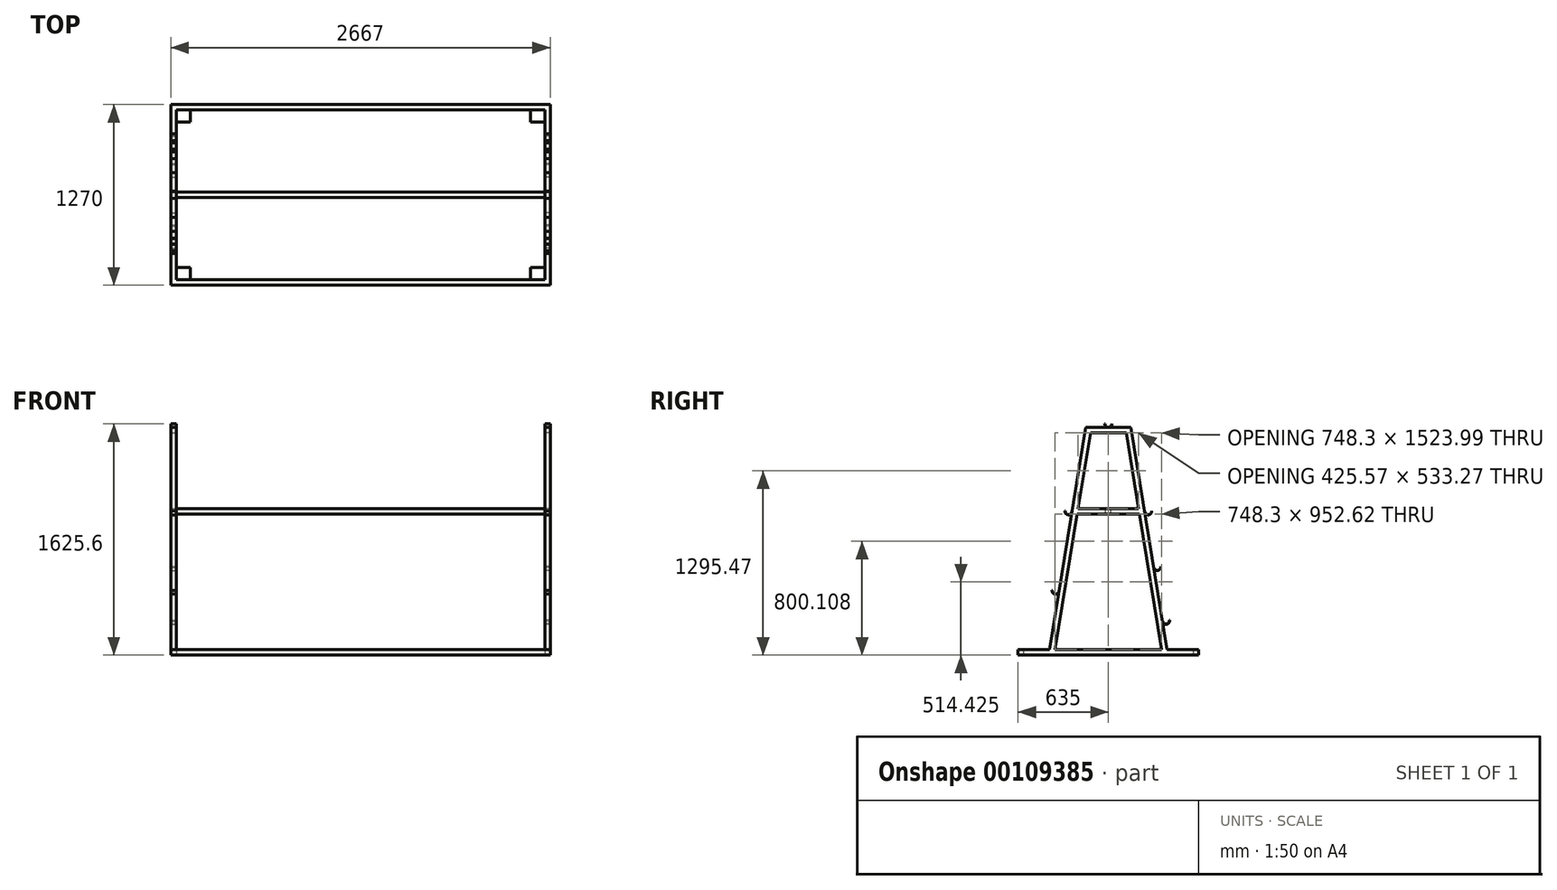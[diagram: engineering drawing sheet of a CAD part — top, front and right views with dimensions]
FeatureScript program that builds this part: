
annotation { "Feature Type Name" : "Feature", "Feature Type Description" : "" }
export const myFeature = defineFeature(function(context is Context, id is Id, definition is map)
    precondition{}
    {
        {
            var Q0;
            Q0=qCreatedBy(makeId("Right.planeOp"),FACE);
            cPlane(context, id + "F0", {"entities" : qUnion([Q0]), "cplaneType" : CPlaneType.OFFSET, "offset" : 1295.4 * mm, "oppositeDirection" : true, "width" : 152.4 * mm, "height" : 152.4 * mm});
        }
        {
            var Q0;
            Q0=qCreatedBy(makeId("Right.planeOp"),FACE);
            var sketch = newSketch(context, id + "F1", { "sketchPlane" : qUnion([Q0])});
            skPoint(sketch, "E0.orphan", {"position": v(0, -38.09) * mm});
            skLineSegment(sketch, "E1.MirrorCS", {"start": v(374.15, 0.02) * mm, "end": v(219, 952.64) * mm});
            skLineSegment(sketch, "E2.trimOffspring", {"start": v(212.79, 990.74) * mm, "end": v(125.93, 1524.01) * mm});
            skLineSegment(sketch, "E3.trimOffspring", {"start": v(412.75, 0.01) * mm, "end": v(635, 0.01) * mm});
            skLineSegment(sketch, "E4.MirrorCS", {"start": v(635, 0.01) * mm, "end": v(635, -38.09) * mm});
            skLineSegment(sketch, "E5", {"start": v(0, 0) * mm, "end": v(0, 1562.11) * mm, "construction": true});
            skLineSegment(sketch, "E6", {"start": v(0, 0.02) * mm, "end": v(374.15, 0.02) * mm});
            skLineSegment(sketch, "E7", {"start": v(158.3, 1562.11) * mm, "end": v(412.75, 0.01) * mm});
            skLineSegment(sketch, "E8.0", {"start": v(0, 1562.11) * mm, "end": v(158.3, 1562.11) * mm});
            skLineSegment(sketch, "E9.trimOffspring", {"start": v(0, 1524) * mm, "end": v(125.93, 1524.01) * mm});
            skLineSegment(sketch, "E10.trimOffspring", {"start": v(0, 990.74) * mm, "end": v(212.79, 990.74) * mm});
            skLineSegment(sketch, "E11.trimOffspring", {"start": v(0, 952.64) * mm, "end": v(219, 952.64) * mm});
            skLineSegment(sketch, "E12", {"start": v(635, -38.09) * mm, "end": v(0, -38.09) * mm});
            skLineSegment(sketch, "E13.trimOffspring", {"start": v(0, 971.7) * mm, "end": v(280.2, 971.7) * mm, "construction": true});
            skLineSegment(sketch, "E14.0", {"start": v(0, 1587.51) * mm, "end": v(158.3, 1587.51) * mm, "construction": true});
            skCircle(sketch, "E15", {"center": v(0, 1587.51) * mm, "radius": 381 * mm, "construction": true});
            skLineSegment(sketch, "E16.0", {"start": v(183.36, 1566.2) * mm, "end": v(437.82, 4.1) * mm, "construction": true});
            skCircle(sketch, "E17", {"center": v(280.2, 971.7) * mm, "radius": 152.4 * mm, "construction": true});
            skLineSegment(sketch, "E18", {"start": v(318.63, 577.82) * mm, "end": v(343.7, 581.9) * mm, "construction": true});
            skCircle(sketch, "E19", {"center": v(343.7, 581.9) * mm, "radius": 152.4 * mm, "construction": true});
            skLineSegment(sketch, "E20", {"start": v(380.13, 200.26) * mm, "end": v(405.2, 204.34) * mm, "construction": true});
            skCircle(sketch, "E21", {"center": v(405.2, 204.34) * mm, "radius": 152.4 * mm, "construction": true});
            skLineSegment(sketch, "E22.MirrorCS", {"start": v(0, 1524) * mm, "end": v(-125.93, 1524.01) * mm});
            skLineSegment(sketch, "E23.MirrorCS", {"start": v(0, 1562.11) * mm, "end": v(-158.3, 1562.11) * mm});
            skLineSegment(sketch, "E24.MirrorCS", {"start": v(-158.3, 1562.11) * mm, "end": v(-412.75, 0.01) * mm});
            skLineSegment(sketch, "E25.MirrorCS", {"start": v(-212.79, 990.74) * mm, "end": v(-125.93, 1524.01) * mm});
            skLineSegment(sketch, "E26.MirrorCS", {"start": v(-183.36, 1566.2) * mm, "end": v(-437.82, 4.1) * mm, "construction": true});
            skLineSegment(sketch, "E27.MirrorCS", {"start": v(0, 990.74) * mm, "end": v(-212.79, 990.74) * mm});
            skLineSegment(sketch, "E28.MirrorCS", {"start": v(0, 971.7) * mm, "end": v(-280.2, 971.7) * mm, "construction": true});
            skLineSegment(sketch, "E29.MirrorCS", {"start": v(0, 952.64) * mm, "end": v(-219, 952.64) * mm});
            skLineSegment(sketch, "E30.MirrorCS", {"start": v(-374.15, 0.02) * mm, "end": v(-219, 952.64) * mm});
            skLineSegment(sketch, "E31.MirrorCS", {"start": v(0, 0.02) * mm, "end": v(-374.15, 0.02) * mm});
            skLineSegment(sketch, "E32.MirrorCS", {"start": v(-412.75, 0.01) * mm, "end": v(-635, 0.01) * mm});
            skLineSegment(sketch, "E33.MirrorCS", {"start": v(-635, -38.09) * mm, "end": v(0, -38.09) * mm});
            skLineSegment(sketch, "E34.MirrorCS", {"start": v(-635, 0.01) * mm, "end": v(-635, -38.09) * mm});
            skCircle(sketch, "E35", {"center": v(-280.2, 971.7) * mm, "radius": 152.4 * mm, "construction": true});
            skLineSegment(sketch, "E36", {"start": v(-345.67, 411.84) * mm, "end": v(-370.74, 415.92) * mm, "construction": true});
            skCircle(sketch, "E37", {"center": v(-370.74, 415.92) * mm, "radius": 304.8 * mm, "construction": true});
            skSolve(sketch);
        }
        {
            var Q0;
            Q0=qSketchRegion(id+"F1",true);
            extrude(context, id + "F2", {"entities" : qUnion([Q0]), "depth" : 38.1 * mm});
        }
        {
            var Q0;
            Q0=makeQuery(id+"F2.opExtrude","SWEPT_BODY",BODY,{"disambiguationData":[OSD([sQuery(id+"F1.wireOp",EDGE,"6WKcqqnf-Tb74-KSXB-T6S0-m3pTTAEzESJp"),sQuery(id+"F1.wireOp",EDGE,"1c0d4eef-4907-47d0-8670-4b10d3ef4e6d0.MirrorCS"),sQuery(id+"F1.wireOp",EDGE,"c0db719b-abba-4705-9bd6-14fd0828cea8.0"),sQuery(id+"F1.wireOp",EDGE,"tZbaEvzS-Xn5Q-mfHi-VXqp-jMpdNEXuN0R4"),sQuery(id+"F1.wireOp",EDGE,"rspVW4E9-zQsA-o8DC-rcqs-QNP9QNG2WVSy"),sQuery(id+"F1.wireOp",EDGE,"08289d95-367d-4b9a-ab30-8cc4f747b8f0.0"),sQuery(id+"F1.wireOp",EDGE,"3ac95e61-57ea-43e8-b189-1b48f2394685.0"),sQuery(id+"F1.wireOp",EDGE,"d8f0bd9f-68f3-4107-a600-d1b0ad9bb81b0.MirrorCS"),sQuery(id+"F1.wireOp",EDGE,"E1.MirrorCS"),sQuery(id+"F1.wireOp",EDGE,"a417d048-553f-458f-8e46-2cb23e010311.0"),sQuery(id+"F1.wireOp",EDGE,"5fd8f543-2721-4fe0-ad3b-1b1c11d777a4.0"),sQuery(id+"F1.wireOp",EDGE,"c230fa98-fb04-4ea0-a6fe-6f0d8f7d4e36.trimOffspring"),sQuery(id+"F1.wireOp",EDGE,"74a05f44-4bf8-40a7-b958-81660b9f7f5f.trimOffspring"),sQuery(id+"F1.wireOp",EDGE,"a848d9df-170e-4563-af66-a8ff7f0327df.trimOffspring"),sQuery(id+"F1.wireOp",EDGE,"E2.trimOffspring"),sQuery(id+"F1.wireOp",EDGE,"84869966-22ca-4afa-a9a6-1a304451bc45.trimOffspring"),sQuery(id+"F1.wireOp",EDGE,"E3.trimOffspring")])]});
            var Q1;
            Q1=qCreatedBy(id+"F0.planeOp",FACE);
            mirror(context, id + "F3", {"entities" : qUnion([Q0]), "mirrorPlane" : qUnion([Q1])});
        }
        {
            var Q0;
            Q0=qCreatedBy(makeId("Right.planeOp"),FACE);
            var sketch = newSketch(context, id + "F4", { "sketchPlane" : qUnion([Q0])});
            skPoint(sketch, "E38.orphan", {"position": v(254.47, 971.68) * mm});
            skArc(sketch, "E39", {"start": v(254.55, 971.69) * mm, "mid": v(281.9, 948.4) * mm, "end": v(305.2, 975.76) * mm});
            skLineSegment(sketch, "E40", {"start": v(254.47, 971.68) * mm, "end": v(256.58, 971.85) * mm});
            skArc(sketch, "E41.0", {"start": v(256.58, 971.85) * mm, "mid": v(281.75, 950.43) * mm, "end": v(303.17, 975.6) * mm});
            skLineSegment(sketch, "E42.trimOffspring", {"start": v(303.17, 975.6) * mm, "end": v(305.2, 975.76) * mm});
            skLineSegment(sketch, "E43", {"start": v(428.26, 208.1) * mm, "end": v(430.27, 208.43) * mm});
            skLineSegment(sketch, "E44.0", {"start": v(183.36, 1566.2) * mm, "end": v(437.82, 4.08) * mm, "construction": true});
            skLineSegment(sketch, "E45", {"start": v(318.63, 577.82) * mm, "end": v(320.63, 578.15) * mm});
            skArc(sketch, "E46", {"start": v(318.63, 577.82) * mm, "mid": v(347.78, 556.83) * mm, "end": v(368.77, 585.99) * mm});
            skArc(sketch, "E47.0", {"start": v(320.63, 578.15) * mm, "mid": v(347.46, 558.84) * mm, "end": v(366.76, 585.66) * mm});
            skLineSegment(sketch, "E48.trimOffspring", {"start": v(366.76, 585.66) * mm, "end": v(368.77, 585.99) * mm});
            skArc(sketch, "E49", {"start": v(380.13, 200.26) * mm, "mid": v(409.28, 179.27) * mm, "end": v(430.27, 208.43) * mm});
            skArc(sketch, "E50.0", {"start": v(382.14, 200.59) * mm, "mid": v(408.96, 181.28) * mm, "end": v(428.26, 208.1) * mm});
            skPoint(sketch, "E51.orphan", {"position": v(380.13, 200.26) * mm});
            skLineSegment(sketch, "E52.trimOffspring", {"start": v(382.14, 200.59) * mm, "end": v(380.13, 200.26) * mm});
            skLineSegment(sketch, "E53.MirrorCS", {"start": v(-254.47, 971.68) * mm, "end": v(-256.58, 971.85) * mm});
            skLineSegment(sketch, "E54.MirrorCS", {"start": v(-303.17, 975.6) * mm, "end": v(-305.2, 975.76) * mm});
            skArc(sketch, "E55.MirrorCS", {"start": v(-256.58, 971.85) * mm, "mid": v(-281.75, 950.43) * mm, "end": v(-303.17, 975.6) * mm});
            skPoint(sketch, "E56.MirrorP", {"position": v(-254.47, 971.68) * mm});
            skArc(sketch, "E57.MirrorCS", {"start": v(-254.55, 971.69) * mm, "mid": v(-281.9, 948.4) * mm, "end": v(-305.2, 975.76) * mm});
            skLineSegment(sketch, "E58.MirrorCS", {"start": v(-183.36, 1566.2) * mm, "end": v(-437.82, 4.08) * mm, "construction": true});
            skLineSegment(sketch, "E59.MirrorCS", {"start": v(-345.33, 413.88) * mm, "end": v(-347.44, 414.05) * mm});
            skLineSegment(sketch, "E60.MirrorCS", {"start": v(-394.03, 417.8) * mm, "end": v(-396.05, 417.95) * mm});
            skArc(sketch, "E61.MirrorCS", {"start": v(-347.44, 414.05) * mm, "mid": v(-372.6, 392.63) * mm, "end": v(-394.03, 417.8) * mm});
            skPoint(sketch, "E62.MirrorP", {"position": v(-345.33, 413.88) * mm});
            skArc(sketch, "E63.MirrorCS", {"start": v(-345.42, 413.88) * mm, "mid": v(-372.77, 390.6) * mm, "end": v(-396.05, 417.95) * mm});
            skArc(sketch, "E64", {"start": v(-25.4, 1587.51) * mm, "mid": v(0, 1562.11) * mm, "end": v(25.4, 1587.51) * mm});
            skArc(sketch, "E65.0", {"start": v(-23.37, 1587.51) * mm, "mid": v(0, 1564.14) * mm, "end": v(23.37, 1587.51) * mm});
            skLineSegment(sketch, "E66", {"start": v(25.4, 1587.51) * mm, "end": v(23.37, 1587.51) * mm});
            skLineSegment(sketch, "E67.trimOffspring", {"start": v(-23.37, 1587.51) * mm, "end": v(-25.4, 1587.51) * mm});
            skSolve(sketch);
        }
        {
            var Q0;
            Q0 = qSketchRegion(id + "F4", true);
            extrude(context, id + "F5", {"entities" : qUnion([Q0]), "depth" : 38.1 * mm});
        }
        {
            var Q0;
            Q0=makeQuery(id+"F5.opExtrude","SWEPT_BODY",BODY,{"disambiguationData":[OSD([sQuery(id+"F4.wireOp",EDGE,"E53.MirrorCS"),sQuery(id+"F4.wireOp",EDGE,"E54.MirrorCS"),sQuery(id+"F4.wireOp",EDGE,"E55.MirrorCS"),sQuery(id+"F4.wireOp",EDGE,"E57.MirrorCS")])]});
            var Q1;
            Q1=makeQuery(id+"F5.opExtrude","SWEPT_BODY",BODY,{"disambiguationData":[OSD([sQuery(id+"F4.wireOp",EDGE,"E59.MirrorCS"),sQuery(id+"F4.wireOp",EDGE,"E60.MirrorCS"),sQuery(id+"F4.wireOp",EDGE,"E61.MirrorCS"),sQuery(id+"F4.wireOp",EDGE,"E63.MirrorCS")])]});
            var Q2;
            Q2=makeQuery(id+"F5.opExtrude","SWEPT_BODY",BODY,{"disambiguationData":[OSD([sQuery(id+"F4.wireOp",EDGE,"E64"),sQuery(id+"F4.wireOp",EDGE,"E65.0"),sQuery(id+"F4.wireOp",EDGE,"E66"),sQuery(id+"F4.wireOp",EDGE,"E67.trimOffspring")])]});
            var Q3;
            Q3=makeQuery(id+"F5.opExtrude","SWEPT_BODY",BODY,{"disambiguationData":[OSD([sQuery(id+"F4.wireOp",EDGE,"E39"),sQuery(id+"F4.wireOp",EDGE,"E40"),sQuery(id+"F4.wireOp",EDGE,"E41.0"),sQuery(id+"F4.wireOp",EDGE,"E42.trimOffspring")])]});
            var Q4;
            Q4=makeQuery(id+"F5.opExtrude","SWEPT_BODY",BODY,{"disambiguationData":[OSD([sQuery(id+"F4.wireOp",EDGE,"E45"),sQuery(id+"F4.wireOp",EDGE,"E46"),sQuery(id+"F4.wireOp",EDGE,"E47.0"),sQuery(id+"F4.wireOp",EDGE,"E48.trimOffspring")])]});
            var Q5;
            Q5=makeQuery(id+"F5.opExtrude","SWEPT_BODY",BODY,{"disambiguationData":[OSD([sQuery(id+"F4.wireOp",EDGE,"E43"),sQuery(id+"F4.wireOp",EDGE,"E49"),sQuery(id+"F4.wireOp",EDGE,"E50.0"),sQuery(id+"F4.wireOp",EDGE,"E52.trimOffspring")])]});
            var Q6;
            Q6=qCreatedBy(id+"F0.planeOp",FACE);
            mirror(context, id + "F6", {"entities" : qUnion([Q0, Q1, Q2, Q3, Q4, Q5]), "mirrorPlane" : qUnion([Q6])});
        }
        {
            var Q0;
            Q0=qCreatedBy(makeId("Right.planeOp"),FACE);
            var sketch = newSketch(context, id + "F7", { "sketchPlane" : qUnion([Q0])});
            skLineSegment(sketch, "E68.0", {"start": v(635, 0.01) * mm, "end": v(635, -38.09) * mm});
            skLineSegment(sketch, "E69", {"start": v(635, 0.01) * mm, "end": v(596.9, 0.01) * mm});
            skLineSegment(sketch, "E70", {"start": v(596.9, 0.01) * mm, "end": v(596.9, -38.09) * mm});
            skLineSegment(sketch, "E71", {"start": v(596.9, -38.09) * mm, "end": v(635, -38.09) * mm});
            skLineSegment(sketch, "E72.0", {"start": v(-635, 0.01) * mm, "end": v(-635, -38.09) * mm});
            skLineSegment(sketch, "E73", {"start": v(-635, 0.01) * mm, "end": v(-596.9, 0.01) * mm});
            skLineSegment(sketch, "E74", {"start": v(-596.9, 0.01) * mm, "end": v(-596.9, -38.09) * mm});
            skLineSegment(sketch, "E75", {"start": v(-596.9, -38.09) * mm, "end": v(-635, -38.09) * mm});
            skSolve(sketch);
        }
        {
            var Q0;
            Q0 = qSketchRegion(id + "F7", true);
            var Q1;
            Q1=makeQuery(id+"F3.opPattern","COPY",FACE,{"derivedFrom":makeQuery(id+"F2.opExtrude","CAP_FACE",FACE,{"disambiguationData":[OSD([sQuery(id+"F1.wireOp",EDGE,"E1.MirrorCS"),sQuery(id+"F1.wireOp",EDGE,"E2.trimOffspring"),sQuery(id+"F1.wireOp",EDGE,"E3.trimOffspring"),sQuery(id+"F1.wireOp",EDGE,"E4.MirrorCS"),sQuery(id+"F1.wireOp",EDGE,"E6"),sQuery(id+"F1.wireOp",EDGE,"E7"),sQuery(id+"F1.wireOp",EDGE,"E8.0"),sQuery(id+"F1.wireOp",EDGE,"E9.trimOffspring"),sQuery(id+"F1.wireOp",EDGE,"E10.trimOffspring"),sQuery(id+"F1.wireOp",EDGE,"E11.trimOffspring"),sQuery(id+"F1.wireOp",EDGE,"E12"),sQuery(id+"F1.wireOp",EDGE,"E22.MirrorCS"),sQuery(id+"F1.wireOp",EDGE,"E23.MirrorCS"),sQuery(id+"F1.wireOp",EDGE,"E24.MirrorCS"),sQuery(id+"F1.wireOp",EDGE,"E25.MirrorCS"),sQuery(id+"F1.wireOp",EDGE,"E27.MirrorCS"),sQuery(id+"F1.wireOp",EDGE,"E29.MirrorCS"),sQuery(id+"F1.wireOp",EDGE,"E30.MirrorCS"),sQuery(id+"F1.wireOp",EDGE,"E31.MirrorCS"),sQuery(id+"F1.wireOp",EDGE,"E32.MirrorCS"),sQuery(id+"F1.wireOp",EDGE,"E33.MirrorCS"),sQuery(id+"F1.wireOp",EDGE,"E34.MirrorCS")])],"isStart":true}),"instanceName":"1"});
            extrude(context, id + "F8", {"entities" : qUnion([Q0]), "operationType" : NewBodyOperationType.ADD, "endBound" : BoundingType.UP_TO_SURFACE, "oppositeDirection" : true, "endBoundEntityFace" : qUnion([Q1]), "depth" : 25.4 * mm});
        }
        {
            var Q0;
            Q0=qCreatedBy(makeId("Right.planeOp"),FACE);
            var sketch = newSketch(context, id + "F9", { "sketchPlane" : qUnion([Q0])});
            skPoint(sketch, "E76.orphan", {"position": v(212.78, 990.73) * mm});
            skPoint(sketch, "E77.orphan", {"position": v(-214.59, 990.73) * mm});
            skLineSegment(sketch, "E78.0", {"start": v(0, 990.74) * mm, "end": v(19.05, 990.74) * mm});
            skLineSegment(sketch, "E79.0", {"start": v(0, 952.64) * mm, "end": v(19.05, 952.64) * mm});
            skLineSegment(sketch, "E80.0", {"start": v(0, 0) * mm, "end": v(0, 1562.11) * mm, "construction": true});
            skLineSegment(sketch, "E81.0", {"start": v(19.05, 952.64) * mm, "end": v(19.05, 990.74) * mm});
            skPoint(sketch, "E82.orphan", {"position": v(212.79, 990.74) * mm});
            skLineSegment(sketch, "E83.MirrorCS", {"start": v(0, 990.74) * mm, "end": v(-19.05, 990.74) * mm});
            skLineSegment(sketch, "E84.MirrorCS", {"start": v(0, 952.64) * mm, "end": v(-19.05, 952.64) * mm});
            skLineSegment(sketch, "E85.MirrorCS", {"start": v(-19.05, 952.64) * mm, "end": v(-19.05, 990.74) * mm});
            skSolve(sketch);
        }
        {
            var Q0;
            Q0 = qSketchRegion(id + "F9", true);
            var Q1;
            Q1=sQuery(id+"F9.wireOp",EDGE,"quJjRLTo-BCDk-AKOd-081C-b5ZIL8STPj5j");
            var Q2;
            Q2=makeQuery(id+"F3.opPattern","COPY",FACE,{"derivedFrom":makeQuery(id+"F2.opExtrude","CAP_FACE",FACE,{"disambiguationData":[OSD([sQuery(id+"F1.wireOp",EDGE,"3ac95e61-57ea-43e8-b189-1b48f2394685.0"),sQuery(id+"F1.wireOp",EDGE,"E1.MirrorCS"),sQuery(id+"F1.wireOp",EDGE,"a417d048-553f-458f-8e46-2cb23e010311.0"),sQuery(id+"F1.wireOp",EDGE,"74a05f44-4bf8-40a7-b958-81660b9f7f5f.trimOffspring"),sQuery(id+"F1.wireOp",EDGE,"a848d9df-170e-4563-af66-a8ff7f0327df.trimOffspring"),sQuery(id+"F1.wireOp",EDGE,"E2.trimOffspring"),sQuery(id+"F1.wireOp",EDGE,"84869966-22ca-4afa-a9a6-1a304451bc45.trimOffspring"),sQuery(id+"F1.wireOp",EDGE,"E3.trimOffspring"),sQuery(id+"F1.wireOp",EDGE,"aNLPhnuB-j6Qy-myk6-tE3M-mN8yZFwiaMap"),sQuery(id+"F1.wireOp",EDGE,"E4.MirrorCS"),sQuery(id+"F1.wireOp",EDGE,"E6"),sQuery(id+"F1.wireOp",EDGE,"xx0CWxqa-nlQP-PgLY-QHwu-dRm1aQXRsNjU"),sQuery(id+"F1.wireOp",EDGE,"E7"),sQuery(id+"F1.wireOp",EDGE,"36GJCszI-Vl5h-sBs6-VTrY-JbHhggqGYl6a"),sQuery(id+"F1.wireOp",EDGE,"x8OdzhxH-0YFc-dZkW-6ny1-HY3YuU4w8q9O"),sQuery(id+"F1.wireOp",EDGE,"9l2WjKLx-MVRy-baPk-qY3i-FHcP7m6FzNa4")])],"isStart":true}),"instanceName":"1"});
            extrude(context, id + "F10", {"entities" : qUnion([Q0]), "operationType" : NewBodyOperationType.ADD, "surfaceEntities" : qUnion([Q1]), "endBound" : BoundingType.UP_TO_SURFACE, "oppositeDirection" : true, "endBoundEntityFace" : qUnion([Q2]), "depth" : 25.4 * mm});
        }
        {
            var Q0;
            {var subQ0=makeQuery(id+"F2.opExtrude","SWEPT_FACE",FACE,{"disambiguationData":[OSD([sQuery(id+"F1.wireOp",EDGE,"9l2WjKLx-MVRy-baPk-qY3i-FHcP7m6FzNa4")])]});Q0=makeQuery(id+"F8.boolean.opBoolean","MERGE",FACE,{"derivedFrom":[subQ0,makeQuery(id+"F3.opPattern","COPY",FACE,{"derivedFrom":subQ0,"instanceName":"1"}),makeQuery(id+"F8.opExtrude","SWEPT_FACE",FACE,{"disambiguationData":[OSD([sQuery(id+"F7.wireOp",EDGE,"a6yDBh03-l4AM-VH5k-SBzY-U7uwqtBh996M")])]}),makeQuery(id+"F8.opExtrude","SWEPT_FACE",FACE,{"disambiguationData":[OSD([sQuery(id+"F7.wireOp",EDGE,"E71")])]})]});}
            cPlane(context, id + "F11", {"entities" : qUnion([Q0]), "cplaneType" : CPlaneType.OFFSET, "offset" : 0 * mm, "width" : 152.4 * mm, "height" : 152.4 * mm});
        }
        {
            var Q0;
            Q0=qCreatedBy(id+"F11.planeOp",FACE);
            var sketch = newSketch(context, id + "F12", { "sketchPlane" : qUnion([Q0])});
            skLineSegment(sketch, "E86.0", {"start": v(-100.01, -596.9) * mm, "end": v(0, -596.9) * mm});
            skLineSegment(sketch, "E87", {"start": v(0, -596.9) * mm, "end": v(0, -511.17) * mm});
            skLineSegment(sketch, "E88", {"start": v(0, -511.17) * mm, "end": v(-100.01, -511.17) * mm});
            skLineSegment(sketch, "E89", {"start": v(-100.01, -511.17) * mm, "end": v(-100.01, -596.9) * mm});
            skPoint(sketch, "E90.orphan", {"position": v(-2590.8, -596.9) * mm});
            skPoint(sketch, "E91.orphan", {"position": v(-2159, 596.9) * mm});
            skLineSegment(sketch, "E92.0", {"start": v(-100.01, 596.9) * mm, "end": v(0, 596.9) * mm});
            skLineSegment(sketch, "E93", {"start": v(0, 596.9) * mm, "end": v(0, 511.17) * mm});
            skLineSegment(sketch, "E94", {"start": v(0, 511.17) * mm, "end": v(-100.01, 511.17) * mm});
            skLineSegment(sketch, "E95", {"start": v(-100.01, 511.17) * mm, "end": v(-100.01, 596.9) * mm});
            skPoint(sketch, "E96.orphan", {"position": v(-2590.8, 596.9) * mm});
            skSolve(sketch);
        }
        {
            var Q0;
            Q0 = qSketchRegion(id + "F12", true);
            extrude(context, id + "F13", {"entities" : qUnion([Q0]), "oppositeDirection" : true, "depth" : 1.52 * mm});
        }
        {
            var Q0;
            Q0=makeQuery(id+"F13.opExtrude","SWEPT_BODY",BODY,{"disambiguationData":[OSD([sQuery(id+"F12.wireOp",EDGE,"E86.0"),sQuery(id+"F12.wireOp",EDGE,"E87"),sQuery(id+"F12.wireOp",EDGE,"E88"),sQuery(id+"F12.wireOp",EDGE,"E89")])]});
            var Q1;
            Q1=makeQuery(id+"F13.opExtrude","SWEPT_BODY",BODY,{"disambiguationData":[OSD([sQuery(id+"F12.wireOp",EDGE,"E92.0"),sQuery(id+"F12.wireOp",EDGE,"E93"),sQuery(id+"F12.wireOp",EDGE,"E94"),sQuery(id+"F12.wireOp",EDGE,"E95")])]});
            var Q2;
            Q2=qCreatedBy(id+"F0.planeOp",FACE);
            mirror(context, id + "F14", {"operationType" : NewBodyOperationType.ADD, "entities" : qUnion([Q0, Q1]), "mirrorPlane" : qUnion([Q2])});
        }
    });
